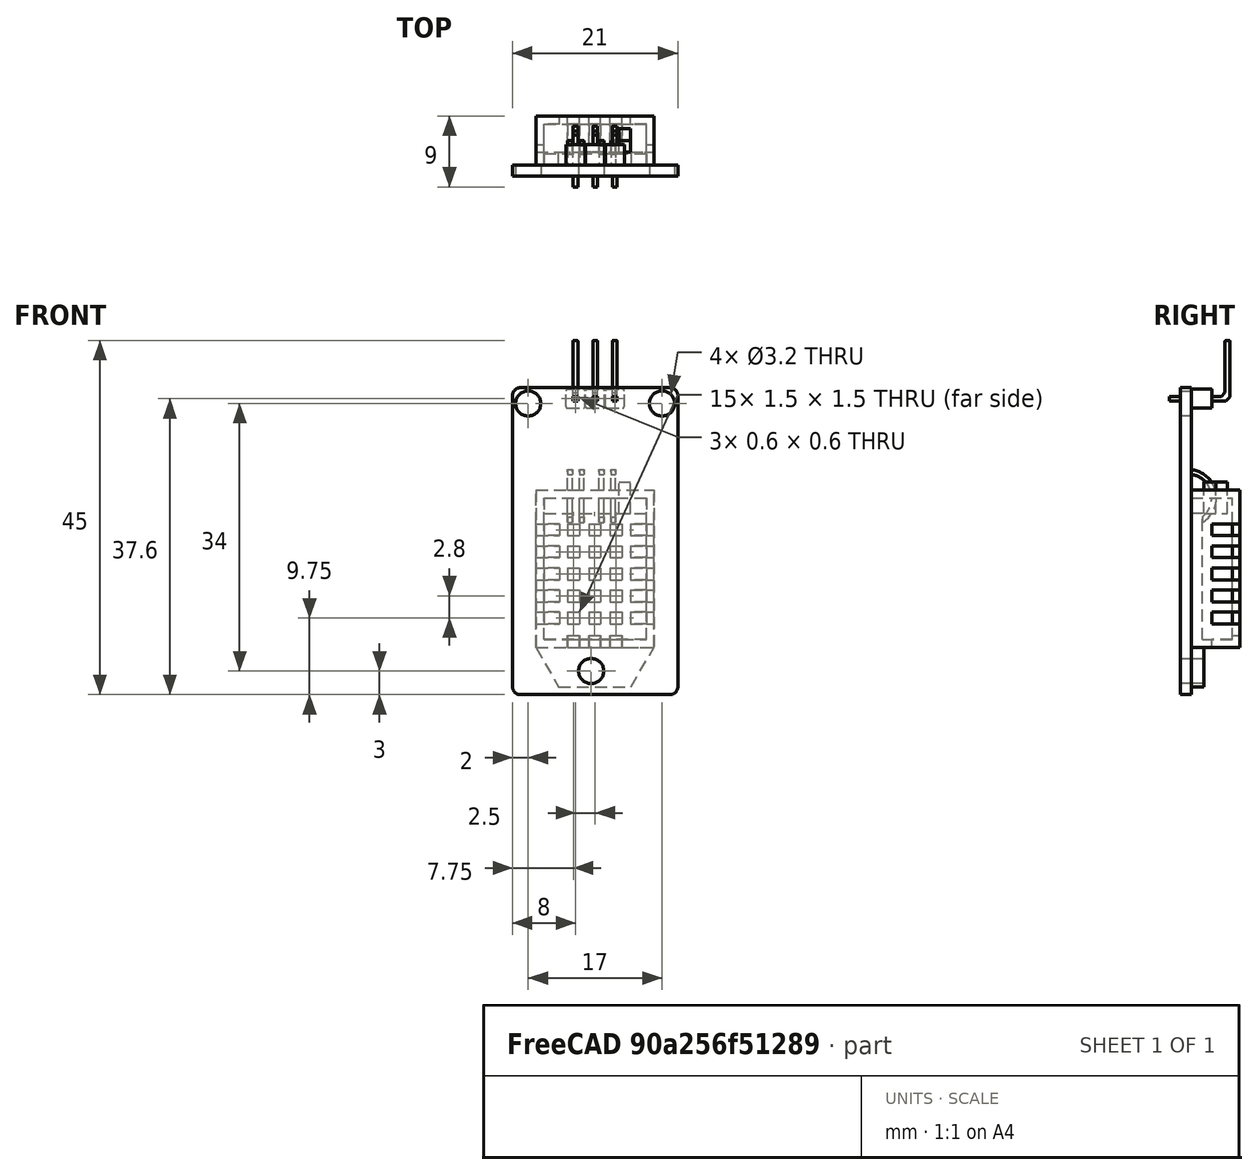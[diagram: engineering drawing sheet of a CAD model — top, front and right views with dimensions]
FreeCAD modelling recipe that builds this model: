
FCSTD DOCUMENT  (FreeCAD 0.20R29603 (Git))
Label: Sensor_DHT22
License: All rights reserved
LicenseURL: http://en.wikipedia.org/wiki/All_rights_reserved
objects: Part::Box×22, Part::Cut×13, Part::MultiFuse×13, Part::Fillet×8, Part::FeaturePython×7, Part::Chamfer×6, Part::Cylinder×4
note: 70 computed .brp shape members not serialized (recipe doc carries the construction recipe); baked Part::Feature solids carry a one-line shape summary decoded from their .brp

FEATURE [Part::Box] Box269  label="Cubo254"
  AttacherType = Attacher::AttachEngine3D
  Height = 1.4
  Length = 39
  Width = 21
FEATURE [Part::Box] Box270  label="Cubo255"
  AttacherType = Attacher::AttachEngine3D
  Height = 7.6
  Length = 20
  Width = 15
FEATURE [Part::Box] Box271  label="Cubo256"
  AttacherType = Attacher::AttachEngine3D
  Height = 4
  Length = 1.5
  Placement = pos=(3,0,4) rot=(0,0,1;0rad)
  Width = 3
FEATURE [Part::FeaturePython] Array005  # Draft array (typed FeaturePython)
  AlwaysSyncPlacement = false
  Angle = 360
  ArrayType = 0
  Axis = (0,0,1)
  Base = -> Box271
  Center = (0,0,0)
  Count = 10
  ExpandArray = false
  Fuse = false
  IntervalAxis = (0,0,0)
  IntervalX = (2.8,0,0)
  IntervalY = (0,12,0)
  IntervalZ = (0,0,100)
  NumberCircles = 3
  NumberPolar = 5
  NumberX = 5
  NumberY = 2
  NumberZ = 1
  PlacementList = 10 placements: [(3,0,4),(3,12,4),(5.8,0,4),(5.8,12,4),(8.6,0,4),(8.6,12,4),(11.4,0,4),(11.4,12,4),(14.2,0,4),(14.2,12,4)]
  RadialDistance = 50
  ScaleList = (10) [(1,1,1),(1,1,1),(1,1,1),(1,1,1),(1,1,1),(1,1,1),(1,1,1),(1,1,1),(1,1,1),(1,1,1)]
  Symmetry = 1
  TangentialDistance = 25
FEATURE [Part::Box] Box272  label="Cubo257"
  AttacherType = Attacher::AttachEngine3D
  Height = 4
  Length = 1.5
  Placement = pos=(3,0,4) rot=(0,0,1;0rad)
  Width = 1.5
FEATURE [Part::FeaturePython] Array006  # Draft array (typed FeaturePython)
  AlwaysSyncPlacement = false
  Angle = 360
  ArrayType = 0
  Axis = (0,0,1)
  Base = -> Box272
  Center = (0,0,0)
  Count = 15
  ExpandArray = false
  Fuse = false
  IntervalAxis = (0,0,0)
  IntervalX = (2.8,0,0)
  IntervalY = (0,2.7,0)
  IntervalZ = (0,0,100)
  NumberCircles = 3
  NumberPolar = 5
  NumberX = 5
  NumberY = 3
  NumberZ = 1
  Placement = pos=(0,4,0) rot=(0,0,1;0rad)
  PlacementList = 15 placements: [(3,0,4),(3,2.7,4),(3,5.4,4),(5.8,0,4),(5.8,2.7,4),(5.8,5.4,4),(8.6,0,4),(8.6,2.7,4),(8.6,5.4,4),(11.4,0,4),(11.4,2.7,4),(11.4,5.4,4),(14.2,0,4),(14.2,2.7,4),(14.2,5.4,4)]
  RadialDistance = 50
  ScaleList = (15) [(1,1,1),(1,1,1),(1,1,1),(1,1,1),(1,1,1),(1,1,1),(1,1,1),(1,1,1),(1,1,1),(1,1,1),(1,1,1),(1,1,1),(1,1,1),(1,1,1),(1,1,1)]
  Symmetry = 1
  TangentialDistance = 25
FEATURE [Part::Box] Box273  label="Cubo258"
  AttacherType = Attacher::AttachEngine3D
  Height = 4
  Length = 1.5
  Placement = pos=(3,0,4) rot=(0,0,1;0rad)
  Width = 1.5
FEATURE [Part::FeaturePython] Array007  # Draft array (typed FeaturePython)
  AlwaysSyncPlacement = false
  Angle = 360
  ArrayType = 0
  Axis = (0,0,1)
  Base = -> Box273
  Center = (0,0,0)
  Count = 3
  ExpandArray = false
  Fuse = false
  IntervalAxis = (0,0,0)
  IntervalX = (2.8,0,0)
  IntervalY = (0,2.7,0)
  IntervalZ = (0,0,100)
  NumberCircles = 3
  NumberPolar = 5
  NumberX = 1
  NumberY = 3
  NumberZ = 1
  Placement = pos=(-3,4,0) rot=(0,0,1;0rad)
  PlacementList = 3 placements: arithmetic series from (3,0,4) step (0,2.7,0) to (3,5.4,4)
  RadialDistance = 50
  ScaleList = (3) [(1,1,1),(1,1,1),(1,1,1)]
  Symmetry = 1
  TangentialDistance = 25
FEATURE [Part::Box] Box274  label="Cubo259"
  AttacherType = Attacher::AttachEngine3D
  Height = 6.6
  Length = 18
  Placement = pos=(1,1,0) rot=(0,0,1;0rad)
  Width = 13
FEATURE [Part::Box] Box275  label="Cubo260"
  AttacherType = Attacher::AttachEngine3D
  Height = 1.6
  Length = 5
  Placement = pos=(1,0,1.4) rot=(0,0,1;0rad)
  Width = 15
FEATURE [Part::Box] Box276  label="Cubo261"
  AttacherType = Attacher::AttachEngine3D
  Height = 1.6
  Length = 5
  Placement = pos=(-2,16.12,1.4) rot=(0,0,-1;1.0472rad)
  Width = 15
FEATURE [Part::Box] Box277  label="Cubo262"
  AttacherType = Attacher::AttachEngine3D
  Height = 1.6
  Length = 5
  Placement = pos=(7,-6.36,1.4) rot=(0,0,1;1.0472rad)
  Width = 15
FEATURE [Part::Box] Box278  label="Cubo263"
  AttacherType = Attacher::AttachEngine3D
  Height = 1.4
  Length = 17
  Placement = pos=(6,3.5,1.4) rot=(0,0,1;0rad)
  Width = 14
FEATURE [Part::Box] Box279  label="Cubo264"
  AttacherType = Attacher::AttachEngine3D
  Height = 2.6
  Length = 2.4
  Placement = pos=(0,0,1.6) rot=(0,0,1;0rad)
  Width = 2.4
FEATURE [Part::Box] Box280  label="Cubo265"
  AttacherType = Attacher::AttachEngine3D
  Height = 7.7
  Length = 0.6
  Width = 0.6
FEATURE [Part::Box] Box281  label="Cubo266"
  AttacherType = Attacher::AttachEngine3D
  Height = 7.7
  Length = 0.6
  Placement = pos=(0,0,7.7) rot=(0,1,0;1.5708rad)
  Width = 0.6
FEATURE [Part::Box] Box282  label="Cubo267"
  AttacherType = Attacher::AttachEngine3D
  Height = 10
  Length = 10
  Placement = pos=(-14,-11,-10) rot=(0,0,1;0rad)
  Width = 10
FEATURE [Part::Box] Box283  label="Cubo268"
  AttacherType = Attacher::AttachEngine3D
  Height = 10
  Length = 10
  Placement = pos=(-14,-11,-10) rot=(0,0,1;0rad)
  Width = 10
FEATURE [Part::Box] Box284  label="Cubo269"
  AttacherType = Attacher::AttachEngine3D
  Height = 10
  Length = 10
  Placement = pos=(20,5,-9) rot=(0,0,1;0rad)
  Width = 10
FEATURE [Part::Box] Box285  label="Cubo270"
  AttacherType = Attacher::AttachEngine3D
  Height = 2.6
  Length = 2.4
  Placement = pos=(0,0,1.6) rot=(0,0,1;0rad)
  Width = 2.4
FEATURE [Part::Box] Box286  label="Cubo271"
  AttacherType = Attacher::AttachEngine3D
  Height = 7.7
  Length = 0.6
  Width = 0.6
FEATURE [Part::Box] Box287  label="Cubo272"
  AttacherType = Attacher::AttachEngine3D
  Height = 7.7
  Length = 0.6
  Placement = pos=(0,0,7.7) rot=(0,1,0;1.5708rad)
  Width = 0.6
FEATURE [Part::Box] Box288  label="Cubo273"
  AttacherType = Attacher::AttachEngine3D
  Height = 2.6
  Length = 2.4
  Placement = pos=(0,0,1.6) rot=(0,0,1;0rad)
  Width = 2.4
FEATURE [Part::Box] Box289  label="Cubo274"
  AttacherType = Attacher::AttachEngine3D
  Height = 7.7
  Length = 0.6
  Width = 0.6
FEATURE [Part::Box] Box290  label="Cubo275"
  AttacherType = Attacher::AttachEngine3D
  Height = 7.7
  Length = 0.6
  Placement = pos=(0,0,7.7) rot=(0,1,0;1.5708rad)
  Width = 0.6
FEATURE [Part::Cut] Cut334
  Base = -> Box270
  Tool = -> Array005
FEATURE [Part::Cut] Cut335
  Base = -> Cut334
  Tool = -> Array006
FEATURE [Part::Cut] Cut336
  Base = -> Cut335
  Tool = -> Array007
FEATURE [Part::Cut] Cut006
  Base = -> Cut336
  Placement = pos=(6,0,0) rot=(0,0,1;0rad)
  Tool = -> Box274
FEATURE [Part::Cut] Cut337
  Base = -> Box275
  Tool = -> Box276
FEATURE [Part::Cut] Cut338
  Base = -> Cut337
  Tool = -> Box277
FEATURE [Part::Cylinder] Cylinder259  label="Cilindro259"
  Angle = 360
  AttacherType = Attacher::AttachEngine3D
  FirstAngle = 0
  Height = 10
  Placement = pos=(37,2,0) rot=(0,0,1;0rad)
  Radius = 1.6
  SecondAngle = 0
FEATURE [Part::Cylinder] Cylinder260  label="Cilindro260"
  Angle = 360
  AttacherType = Attacher::AttachEngine3D
  FirstAngle = 0
  Height = 10
  Placement = pos=(37,19,0) rot=(0,0,1;0rad)
  Radius = 1.6
  SecondAngle = 0
FEATURE [Part::Cylinder] Cylinder261  label="Cilindro261"
  Angle = 360
  AttacherType = Attacher::AttachEngine3D
  FirstAngle = 0
  Height = 10
  Placement = pos=(3,10,0) rot=(0,0,1;0rad)
  Radius = 1.6
  SecondAngle = 0
FEATURE [Part::Cylinder] Cylinder262  label="Cilindro262"
  Angle = 360
  AttacherType = Attacher::AttachEngine3D
  FirstAngle = 0
  Height = 10
  Placement = pos=(3,10,0) rot=(0,0,1;0rad)
  Radius = 1.6
  SecondAngle = 0
FEATURE [Part::Fillet] Fillet209
  Base = -> Box269
  Edges = 3 edges r=1: [Edge3,Edge5,Edge7]
FEATURE [Part::Fillet] Fillet210
  Base = -> Fillet209
  Edges = 1 edges r=1: [Edge2]
FEATURE [Part::Cut] Cut331
  Base = -> Fillet210
  Tool = -> Cylinder259
FEATURE [Part::Cut] Cut332  label="CircuitoImpreso001"
  Base = -> Cut331
  Tool = -> Cylinder260
FEATURE [Part::Cut] Cut333  label="CircuitoImpreso002"
  Base = -> Cut332
  Tool = -> Cylinder261
FEATURE [Part::Fillet] Fillet211  label="BasePlastico003"
  Base = -> Box279
  Edges = 4 edges r=0.2: [Edge1,Edge3,Edge5,Edge7]
FEATURE [Part::Fillet] Fillet213  label="BasePlastico004"
  Base = -> Box285
  Edges = 4 edges r=0.2: [Edge1,Edge3,Edge5,Edge7]
FEATURE [Part::Fillet] Fillet215  label="BasePlastico005"
  Base = -> Box288
  Edges = 4 edges r=0.2: [Edge1,Edge3,Edge5,Edge7]
FEATURE [Part::MultiFuse] Fusion185
  Placement = pos=(0,3,0) rot=(0,0,1;0rad)
  Shapes = -> [Cut006,Cut338]
FEATURE [Part::Cut] Cut339
  Base = -> Fusion185
  Tool = -> Cylinder262
FEATURE [Part::MultiFuse] Fusion186  label="DHT22"
  Shapes = -> [Cut339,Box278]
FEATURE [Part::MultiFuse] Fusion191
  Shapes = -> [Box280,Box281]
FEATURE [Part::Chamfer] Chamfer034
  Base = -> Fusion191
  Edges = 1 edges r=0.5: [Edge9]
FEATURE [Part::Chamfer] Chamfer035
  Base = -> Chamfer034
  Edges = 1 edges r=0.5: [Edge31]
FEATURE [Part::Fillet] Fillet212  label="CuerpoMetal003"
  Base = -> Chamfer035
  Edges = 4 edges r=0.1: [Edge5,Edge8,Edge14,Edge15]
  Placement = pos=(0.9,0.9,-1.2) rot=(0,0,1;0rad)
FEATURE [Part::MultiFuse] Fusion190  label="ConectorMacho003"
  Placement = pos=(36.4,6.8,-0.2) rot=(0,0,1;0rad)
  Shapes = -> [Fillet211,Fillet212]
FEATURE [Part::MultiFuse] Fusion193
  Shapes = -> [Box286,Box287]
FEATURE [Part::Chamfer] Chamfer036
  Base = -> Fusion193
  Edges = 1 edges r=0.5: [Edge9]
FEATURE [Part::Chamfer] Chamfer037
  Base = -> Chamfer036
  Edges = 1 edges r=0.5: [Edge31]
FEATURE [Part::Fillet] Fillet214  label="CuerpoMetal004"
  Base = -> Chamfer037
  Edges = 4 edges r=0.1: [Edge5,Edge8,Edge14,Edge15]
  Placement = pos=(0.9,0.9,-1.2) rot=(0,0,1;0rad)
FEATURE [Part::MultiFuse] Fusion192  label="ConectorMacho004"
  Placement = pos=(36.4,9.3,-0.2) rot=(0,0,1;0rad)
  Shapes = -> [Fillet213,Fillet214]
FEATURE [Part::MultiFuse] Fusion195
  Shapes = -> [Box289,Box290]
FEATURE [Part::Chamfer] Chamfer038
  Base = -> Fusion195
  Edges = 1 edges r=0.5: [Edge9]
FEATURE [Part::Chamfer] Chamfer039
  Base = -> Chamfer038
  Edges = 1 edges r=0.5: [Edge31]
FEATURE [Part::Fillet] Fillet216  label="CuerpoMetal005"
  Base = -> Chamfer039
  Edges = 4 edges r=0.1: [Edge5,Edge8,Edge14,Edge15]
  Placement = pos=(0.9,0.9,-1.2) rot=(0,0,1;0rad)
FEATURE [Part::MultiFuse] Fusion194  label="ConectorMacho005"
  Placement = pos=(36.4,11.8,-0.2) rot=(0,0,1;0rad)
  Shapes = -> [Fillet215,Fillet216]
FEATURE [Part::MultiFuse] Fusion196
  Shapes = -> [Cut333,Fusion186]
FEATURE [Part::FeaturePython] Tube009  # WARN: FeaturePython — macro-defined, semantics opaque (R4)
  AttacherType = Attacher::AttachEngine3D
  Height = 0.6
  InnerRadius = 3
  OuterRadius = 3.6
  Placement = pos=(-12,-5,2) rot=(0,1,0;1.5708rad)
FEATURE [Part::FeaturePython] Tube010  # WARN: FeaturePython — macro-defined, semantics opaque (R4)
  AttacherType = Attacher::AttachEngine3D
  Height = 0.6
  InnerRadius = 3
  OuterRadius = 3.6
  Placement = pos=(-10.5,-5,2) rot=(0,1,0;1.5708rad)
FEATURE [Part::MultiFuse] Fusion187
  Shapes = -> [Tube010,Tube009]
FEATURE [Part::Cut] Cut340
  Base = -> Fusion187
  Placement = pos=(20,19,-1) rot=(0,0,1;1.5708rad)
  Tool = -> Box282
FEATURE [Part::FeaturePython] Tube011  # WARN: FeaturePython — macro-defined, semantics opaque (R4)
  AttacherType = Attacher::AttachEngine3D
  Height = 0.6
  InnerRadius = 3
  OuterRadius = 3.6
  Placement = pos=(-12,-5,2) rot=(0,1,0;1.5708rad)
FEATURE [Part::FeaturePython] Tube012  # WARN: FeaturePython — macro-defined, semantics opaque (R4)
  AttacherType = Attacher::AttachEngine3D
  Height = 0.6
  InnerRadius = 3
  OuterRadius = 3.6
  Placement = pos=(-10.5,-5,2) rot=(0,1,0;1.5708rad)
FEATURE [Part::MultiFuse] Fusion188
  Shapes = -> [Tube012,Tube011]
FEATURE [Part::Cut] Cut341
  Base = -> Fusion188
  Placement = pos=(20,23,-1) rot=(0,0,1;1.5708rad)
  Tool = -> Box283
FEATURE [Part::MultiFuse] Fusion189
  Shapes = -> [Cut340,Cut341]
FEATURE [Part::Cut] Cut342  label="Conectores"
  Base = -> Fusion189
  Tool = -> Box284
FEATURE [Part::MultiFuse] Fusion197  label="Sensor_DHT22"
  Placement = pos=(-10.5,-3,-19) rot=(0.57735,0.57735,0.57735;4.18879rad)
  Shapes = -> [Fusion196,Fusion194,Fusion192,Fusion190,Cut342]
